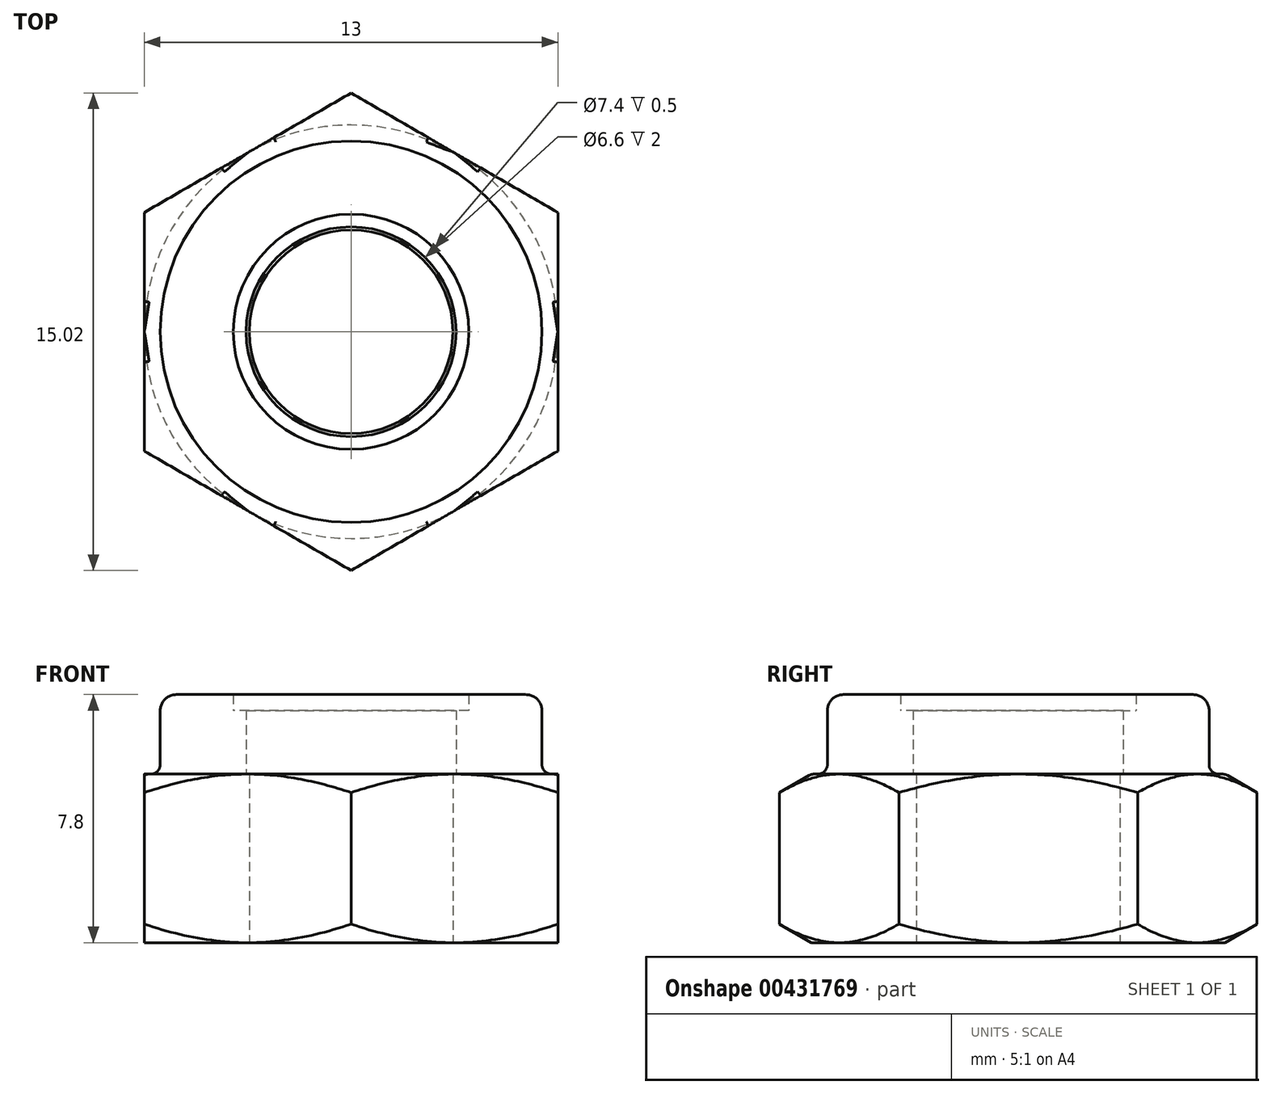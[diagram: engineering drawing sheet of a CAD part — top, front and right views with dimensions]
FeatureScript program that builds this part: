
annotation { "Feature Type Name" : "Feature", "Feature Type Description" : "" }
export const myFeature = defineFeature(function(context is Context, id is Id, definition is map)
    precondition{}
    {
        {
            var Q0;
            Q0=qCreatedBy(makeId("Top.planeOp"),FACE);
            var sketch = newSketch(context, id + "F0", { "sketchPlane" : qUnion([Q0])});
            skCircle(sketch, "E0.cCircle", {"center": v(0, 0) * mm, "radius": 6.5 * mm, "construction": true});
            skLineSegment(sketch, "E0.0", {"start": v(6.5, 3.75) * mm, "end": v(6.5, -3.75) * mm});
            skLineSegment(sketch, "E0.1", {"start": v(6.5, -3.75) * mm, "end": v(0, -7.5) * mm});
            skLineSegment(sketch, "E0.2", {"start": v(0, -7.5) * mm, "end": v(-6.5, -3.75) * mm});
            skLineSegment(sketch, "E0.3", {"start": v(-6.5, -3.75) * mm, "end": v(-6.5, 3.75) * mm});
            skLineSegment(sketch, "E0.4", {"start": v(-6.5, 3.75) * mm, "end": v(0, 7.5) * mm});
            skLineSegment(sketch, "E0.5", {"start": v(0, 7.5) * mm, "end": v(6.5, 3.75) * mm});
            skPoint(sketch, "E0.0.midPoint", {"position": v(6.5, 0) * mm});
            skCircle(sketch, "E1", {"center": v(0, 0) * mm, "radius": 3.2 * mm});
            skSolve(sketch);
        }
        {
            var Q0;
            Q0 = qSketchRegion(id + "F0", true);
            extrude(context, id + "F1", {"entities" : qUnion([Q0]), "depth" : 5.3 * mm});
        }
        {
            var Q0;
            Q0=qCreatedBy(makeId("Front.planeOp"),FACE);
            var sketch = newSketch(context, id + "F2", { "sketchPlane" : qUnion([Q0])});
            skLineSegment(sketch, "E2", {"start": v(6.5, 5.3) * mm, "end": v(10.27, 5.3) * mm});
            skLineSegment(sketch, "E3", {"start": v(10.27, 5.3) * mm, "end": v(10.27, 3.13) * mm});
            skLineSegment(sketch, "E4", {"start": v(10.27, 3.13) * mm, "end": v(6.5, 5.3) * mm});
            skLineSegment(sketch, "E5", {"start": v(6.5, 0) * mm, "end": v(9.95, 0) * mm});
            skLineSegment(sketch, "E6", {"start": v(9.95, 0) * mm, "end": v(9.95, 2) * mm});
            skLineSegment(sketch, "E7", {"start": v(9.95, 2) * mm, "end": v(6.5, 0) * mm});
            skLineSegment(sketch, "E8", {"start": v(0, 0) * mm, "end": v(0, 8.72) * mm, "construction": true});
            skSolve(sketch);
        }
        {
            var Q0;
            Q0=makeQuery(id+"F2.imprint","IMPRINT",FACE,{"disambiguationData":[TD([[makeQuery(id+"F2.imprint","IMPRINT",EDGE,{"derivedFrom":sQuery(id+"F2.wireOp",EDGE,"E2")}),-1.0]])]});
            var Q1;
            Q1=makeQuery(id+"F2.imprint","IMPRINT",FACE,{"disambiguationData":[TD([[makeQuery(id+"F2.imprint","IMPRINT",EDGE,{"derivedFrom":sQuery(id+"F2.wireOp",EDGE,"E5")}),1.0]])]});
            var Q2;
            Q2=sQuery(id+"F2.wireOp",EDGE,"E8");
            revolve(context, id + "F3", {"operationType" : NewBodyOperationType.REMOVE, "entities" : qUnion([Q0, Q1]), "axis" : qUnion([Q2]), "revolveType" : RevolveType.FULL, "oppositeDirection" : true});
        }
        {
            var Q0;
            Q0=qCreatedBy(makeId("Front.planeOp"),FACE);
            var sketch = newSketch(context, id + "F4", { "sketchPlane" : qUnion([Q0])});
            skLineSegment(sketch, "E9", {"start": v(-6, 5.3) * mm, "end": v(-6, 7.3) * mm});
            skLineSegment(sketch, "E10", {"start": v(-5.5, 7.8) * mm, "end": v(-3.7, 7.8) * mm});
            skArc(sketch, "E11", {"start": v(-6, 7.3) * mm, "mid": v(-5.85, 7.65) * mm, "end": v(-5.5, 7.8) * mm});
            skLineSegment(sketch, "E12", {"start": v(-3.7, 7.8) * mm, "end": v(-3.7, 5.3) * mm});
            skLineSegment(sketch, "E13", {"start": v(-6, 5.3) * mm, "end": v(-3.7, 5.3) * mm});
            skSolve(sketch);
        }
        {
            var Q0;
            Q0=makeQuery(id+"F4.imprint","IMPRINT",FACE,{"disambiguationData":[TD([[makeQuery(id+"F4.imprint","IMPRINT",EDGE,{"derivedFrom":sQuery(id+"F4.wireOp",EDGE,"E9")}),-1.0]])]});
            var Q1;
            Q1=sQuery(id+"F2.wireOp",EDGE,"E8");
            revolve(context, id + "F5", {"operationType" : NewBodyOperationType.ADD, "entities" : qUnion([Q0]), "axis" : qUnion([Q1]), "revolveType" : RevolveType.FULL});
        }
        {
            var Q0;
            Q0=makeQuery(id+"F5.opRevolve","SWEPT_FACE",FACE,{"disambiguationData":[OSD([sQuery(id+"F4.wireOp",EDGE,"E9")])]});
            var Q1;
            {var subQ0=sQuery(id+"F0.wireOp",EDGE,"E0.0");var subQ1=makeQuery(id+"F1.opExtrude","SWEPT_FACE",FACE,{"disambiguationData":[OSD([subQ0])]});var subQ3=sQuery(id+"F0.wireOp",EDGE,"E0.5");var subQ4=sQuery(id+"F0.wireOp",EDGE,"E0.4");var subQ5=sQuery(id+"F0.wireOp",EDGE,"E0.3");var subQ6=sQuery(id+"F0.wireOp",EDGE,"E0.2");var subQ7=sQuery(id+"F0.wireOp",EDGE,"E0.1");var subQ8=makeQuery(id+"F1.opExtrude","CAP_FACE",FACE,{"disambiguationData":[OSD([subQ0,subQ7,subQ6,subQ5,subQ4,subQ3,sQuery(id+"F0.wireOp",EDGE,"E1")])],"isStart":false});Q1=makeQuery(id+"F5.boolean.opBoolean","SPLIT",FACE,{"disambiguationData":[TD([subQ1])],"derivedFrom":subQ8});}
            fillet(context, id + "F6", {"entities" : qUnion([Q0, Q1]), "radius" : .3 * mm, "tangentPropagation" : true, "allowEdgeOverflow" : false});
        }
        {
            var Q0;
            Q0=qCreatedBy(makeId("Front.planeOp"),FACE);
            var sketch = newSketch(context, id + "F7", { "sketchPlane" : qUnion([Q0])});
            skLineSegment(sketch, "E14", {"start": v(-3.7, 5.3) * mm, "end": v(-3.7, 7.3) * mm});
            skLineSegment(sketch, "E15", {"start": v(-3.7, 7.3) * mm, "end": v(-3.3, 7.3) * mm});
            skLineSegment(sketch, "E16", {"start": v(-3.3, 7.3) * mm, "end": v(-3.3, 5.3) * mm});
            skLineSegment(sketch, "E17", {"start": v(-3.3, 5.3) * mm, "end": v(-3.7, 5.3) * mm});
            skSolve(sketch);
        }
        {
            var Q0;
            Q0=makeQuery(id+"F7.imprint","IMPRINT",FACE,{"disambiguationData":[TD([[makeQuery(id+"F7.imprint","IMPRINT",EDGE,{"derivedFrom":sQuery(id+"F7.wireOp",EDGE,"E14")}),-1.0]])]});
            var Q1;
            Q1=sQuery(id+"F2.wireOp",EDGE,"E8");
            revolve(context, id + "F8", {"operationType" : NewBodyOperationType.ADD, "entities" : qUnion([Q0]), "axis" : qUnion([Q1]), "revolveType" : RevolveType.FULL});
        }
    });
